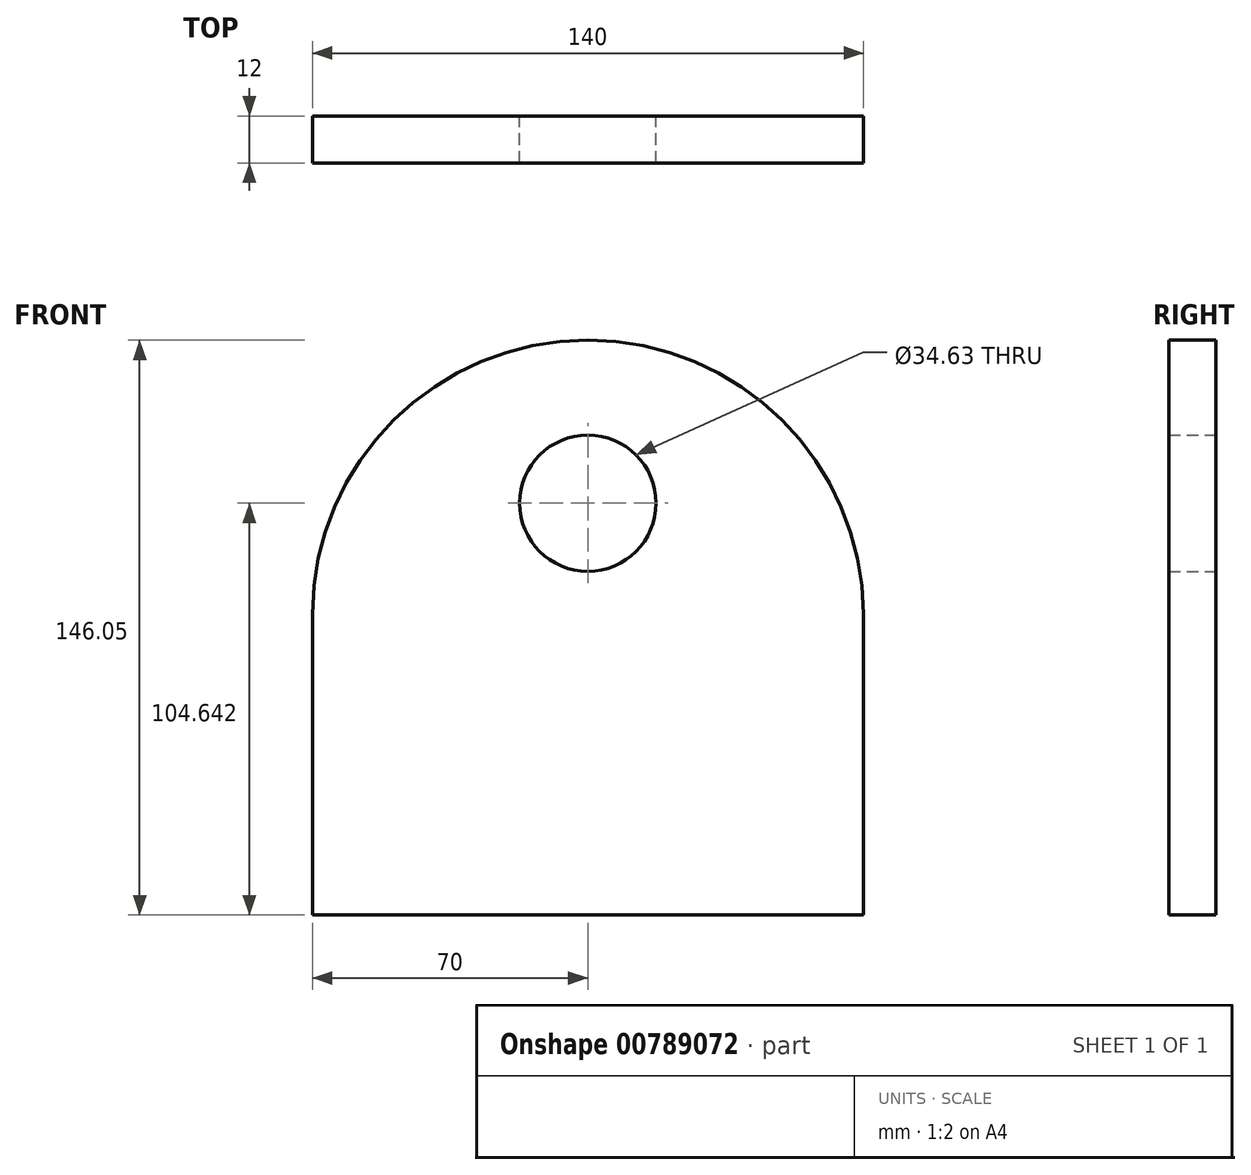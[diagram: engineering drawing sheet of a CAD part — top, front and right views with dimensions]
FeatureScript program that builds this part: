
annotation { "Feature Type Name" : "Feature", "Feature Type Description" : "" }
export const myFeature = defineFeature(function(context is Context, id is Id, definition is map)
    precondition{}
    {
        {
            var Q0;
            Q0=qCreatedBy(makeId("Front.planeOp"),FACE);
            var sketch = newSketch(context, id + "F0", { "sketchPlane" : qUnion([Q0])});
            skLineSegment(sketch, "E0.bottom", {"start": v(0, 0) * mm, "end": v(140, 0) * mm});
            skLineSegment(sketch, "E0.left", {"start": v(0, 0) * mm, "end": v(0, 76.56) * mm});
            skLineSegment(sketch, "E0.right", {"start": v(140, 0) * mm, "end": v(140, 76.56) * mm});
            skArc(sketch, "E1", {"start": v(140, 76.56) * mm, "mid": v(70, 146.05) * mm, "end": v(0, 76.56) * mm});
            skCircle(sketch, "E2", {"center": v(70, 104.64) * mm, "radius": 17.32 * mm});
            skPoint(sketch, "E3.orphan", {"position": v(0, 153.12) * mm});
            skPoint(sketch, "E4.orphan", {"position": v(140, 153.12) * mm});
            skSolve(sketch);
        }
        {
            var Q0;
            Q0=makeQuery(id+"F0.imprint","IMPRINT",FACE,{"disambiguationData":[TD([[makeQuery(id+"F0.imprint","IMPRINT",EDGE,{"derivedFrom":sQuery(id+"F0.wireOp",EDGE,"E0.bottom")}),1.0]])]});
            extrude(context, id + "F1", {"entities" : qUnion([Q0]), "depth" : 12 * mm, "offsetDistance" : 25 * mm});
        }
    });
